# Revit family: USYSTEMS_Проводной термостат цифровой_TW-9
name_source: partatom
category: Датчики
units: mm (PartAtom-declared; Revit-internal decimal feet)

## family parameters
Всегда вертикально = Да
На основе рабочей плоскости = Нет
Общий = Нет
При загрузке вырезать с полостями = Нет
Размер круглого соединителя = Использовать диаметр
Сохранять ориентацию аннотаций = Нет
Тип детали = Нормальный
Точка расчета площади = Нет

## types (2) — shared parameters
ADSK_Версия Revit = 2019
ADSK_Единица измерения = шт
ADSK_Завод-изготовитель = USYSTEMS
ADSK_Количество = 1
ADSK_Количество фаз = 1
ADSK_Напряжение = 230 В
Высота экрана = 49 мм
Кнопки = USYSTEMS_Кнопки
Отображение на экране = USYSTEMS_Отображение на экране
Отступ длины задней части = 4 мм
Привязка плоскости экраа = 9 мм
Радиус сопряжения = 6 мм
Сторона задней части = 50 мм
Сторона корпуса = 85 мм
Толшина жкрана = 2 мм
Толщина передней части = 13 мм
Тощина залней части = 35 мм
Ширина экрана = 63 мм
Экран = USYSTEMS_Экран
zero-valued in all types: ADSK_Масса

## per-type parameters (varying)
| type | ADSK_Код изделия | ADSK_Марка | ADSK_Наименование | Корпус |
| TW-9 белый | 1137048 | Проводной термостат цифровой TW-9 белый | USYSTEMS проводной термостат цифровой TW-9 белый | USYSTEMS_Пластик белый |
| TW-9 черный | 1137049 | Проводной термостат цифровой TW-9 черный | USYSTEMS проводной термостат цифровой TW-9 черный | USYSTEMS_Пластик черный |
